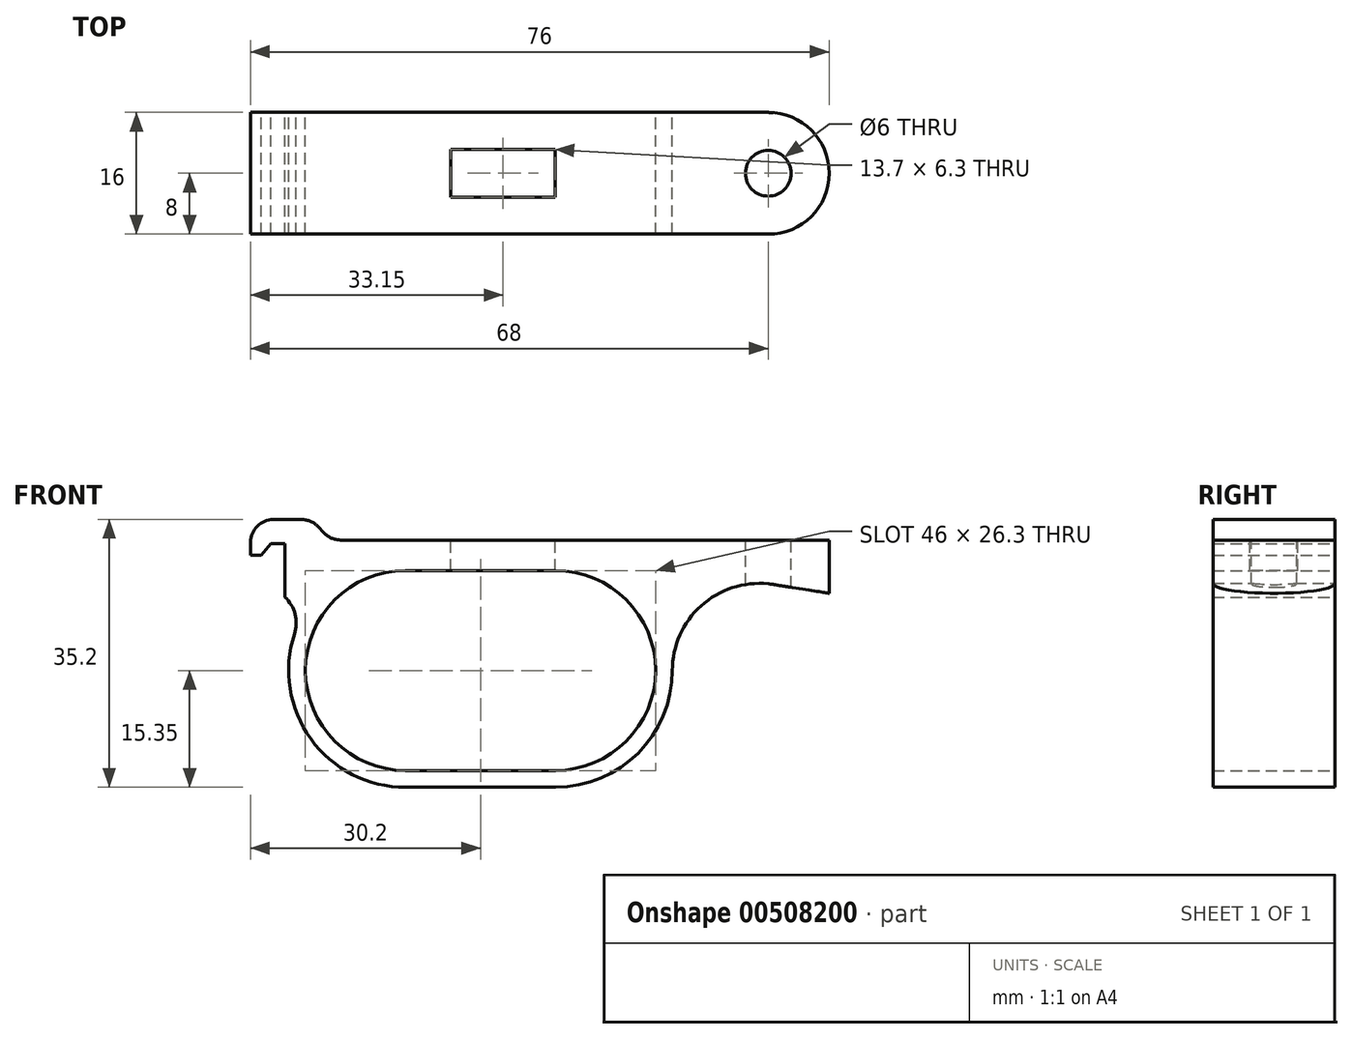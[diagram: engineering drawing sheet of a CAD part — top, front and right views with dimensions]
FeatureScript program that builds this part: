
annotation { "Feature Type Name" : "Feature", "Feature Type Description" : "" }
export const myFeature = defineFeature(function(context is Context, id is Id, definition is map)
    precondition{}
    {
        {
            var Q0;
            Q0=qCreatedBy(makeId("Front.planeOp"),FACE);
            var sketch = newSketch(context, id + "F0", { "sketchPlane" : qUnion([Q0])});
            skArc(sketch, "E0", {"start": v(-9.85, 13.15) * mm, "mid": v(-23, 0) * mm, "end": v(-9.85, -13.15) * mm});
            skArc(sketch, "E1", {"start": v(9.85, -13.15) * mm, "mid": v(23, 0) * mm, "end": v(9.85, 13.15) * mm});
            skLineSegment(sketch, "E2", {"start": v(-9.85, 13.15) * mm, "end": v(9.85, 13.15) * mm});
            skLineSegment(sketch, "E3", {"start": v(9.85, -13.15) * mm, "end": v(-9.85, -13.15) * mm});
            skLineSegment(sketch, "E4", {"start": v(-9.85, 0) * mm, "end": v(9.85, 0) * mm, "construction": true});
            skArc(sketch, "E5.0", {"start": v(-24.43, 4.8) * mm, "mid": v(-22.28, -9) * mm, "end": v(-9.85, -15.35) * mm});
            skLineSegment(sketch, "E5.1", {"start": v(-19.7, 17.15) * mm, "end": v(45.8, 17.15) * mm});
            skArc(sketch, "E5.2", {"start": v(9.85, -15.35) * mm, "mid": v(20.7, -10.85) * mm, "end": v(25.2, 0) * mm});
            skLineSegment(sketch, "E5.3", {"start": v(9.85, -15.35) * mm, "end": v(-9.85, -15.35) * mm});
            skArc(sketch, "E6", {"start": v(38.43, 11.31) * mm, "mid": v(29.21, 8.7) * mm, "end": v(25.2, 0) * mm});
            skLineSegment(sketch, "E7", {"start": v(-25.7, 9.65) * mm, "end": v(-25.7, 16.65) * mm});
            skLineSegment(sketch, "E8", {"start": v(45.8, 17.15) * mm, "end": v(45.8, 10.15) * mm});
            skLineSegment(sketch, "E9", {"start": v(38.43, 11.31) * mm, "end": v(45.8, 10.15) * mm});
            skLineSegment(sketch, "E10", {"start": v(-19.7, 17.15) * mm, "end": v(-22.2, 19.85) * mm});
            skLineSegment(sketch, "E11", {"start": v(-22.2, 19.85) * mm, "end": v(-30.2, 19.85) * mm});
            skLineSegment(sketch, "E12", {"start": v(-30.2, 19.85) * mm, "end": v(-30.2, 15.15) * mm});
            skLineSegment(sketch, "E13", {"start": v(-30.2, 15.15) * mm, "end": v(-28.8, 15.15) * mm});
            skLineSegment(sketch, "E14", {"start": v(-28.8, 15.15) * mm, "end": v(-27.5, 16.65) * mm});
            skLineSegment(sketch, "E15", {"start": v(-27.5, 16.65) * mm, "end": v(-25.7, 16.65) * mm});
            skArc(sketch, "E16", {"start": v(-24.43, 4.8) * mm, "mid": v(-24.35, 7.41) * mm, "end": v(-25.7, 9.65) * mm});
            skSolve(sketch);
        }
        {
            var Q0;
            Q0 = qSketchRegion(id + "F0", true);
            extrude(context, id + "F1", {"entities" : qUnion([Q0]), "depth" : 16 * mm, "offsetDistance" : 25 * mm});
        }
        {
            var Q0;
            Q0=makeQuery(id+"F1.opExtrude","SWEPT_EDGE",EDGE,{"disambiguationData":[OSD([sQuery(id+"F0.wireOp",EDGE,"E11"),sQuery(id+"F0.wireOp",EDGE,"E12")])]});
            var Q1;
            Q1=makeQuery(id+"F1.opExtrude","SWEPT_EDGE",EDGE,{"disambiguationData":[OSD([sQuery(id+"F0.wireOp",EDGE,"E10"),sQuery(id+"F0.wireOp",EDGE,"E11")])]});
            var Q2;
            Q2=makeQuery(id+"F1.opExtrude","SWEPT_EDGE",EDGE,{"disambiguationData":[OSD([sQuery(id+"F0.wireOp",EDGE,"E5.1"),sQuery(id+"F0.wireOp",EDGE,"E10")])]});
            fillet(context, id + "F2", {"entities" : qUnion([Q0, Q1, Q2]), "tangentPropagation" : true, "radius" : 3 * mm, "defaultsChanged" : false, "vertexSettings" : [], "allowEdgeOverflow" : false});
        }
        {
            var Q0;
            Q0=makeQuery(id+"F1.opExtrude","CAP_EDGE",EDGE,{"disambiguationData":[OSD([sQuery(id+"F0.wireOp",EDGE,"E8")])],"isStart":false});
            var Q1;
            Q1=makeQuery(id+"F1.opExtrude","CAP_EDGE",EDGE,{"disambiguationData":[OSD([sQuery(id+"F0.wireOp",EDGE,"E8")])],"isStart":true});
            fillet(context, id + "F3", {"entities" : qUnion([Q0, Q1]), "tangentPropagation" : true, "radius" : 8 * mm, "defaultsChanged" : true, "vertexSettings" : [], "allowEdgeOverflow" : false});
        }
        {
            var Q0;
            Q0=makeQuery(id+"F1.opExtrude","SWEPT_FACE",FACE,{"disambiguationData":[OSD([sQuery(id+"F0.wireOp",EDGE,"E5.1")])]});
            var sketch = newSketch(context, id + "F4", { "sketchPlane" : qUnion([Q0])});
            skCircle(sketch, "E17", {"center": v(37.8, -8) * mm, "radius": 3 * mm});
            skPoint(sketch, "E17.centerSnap0", {"position": v(45.8, -8) * mm});
            skLineSegment(sketch, "E18.bottom", {"start": v(-3.9, -4.85) * mm, "end": v(9.8, -4.85) * mm});
            skLineSegment(sketch, "E18.top", {"start": v(-3.9, -11.15) * mm, "end": v(9.8, -11.15) * mm});
            skLineSegment(sketch, "E18.left", {"start": v(-3.9, -4.85) * mm, "end": v(-3.9, -11.15) * mm});
            skLineSegment(sketch, "E18.right", {"start": v(9.8, -4.85) * mm, "end": v(9.8, -11.15) * mm});
            skPoint(sketch, "E18.middle", {"position": v(2.95, -8) * mm});
            skSolve(sketch);
        }
        {
            var Q0;
            Q0 = qSketchRegion(id + "F4", true);
            extrude(context, id + "F5", {"entities" : qUnion([Q0]), "operationType" : NewBodyOperationType.REMOVE, "oppositeDirection" : true, "depth" : 10 * mm, "offsetDistance" : 25 * mm});
        }
    });
